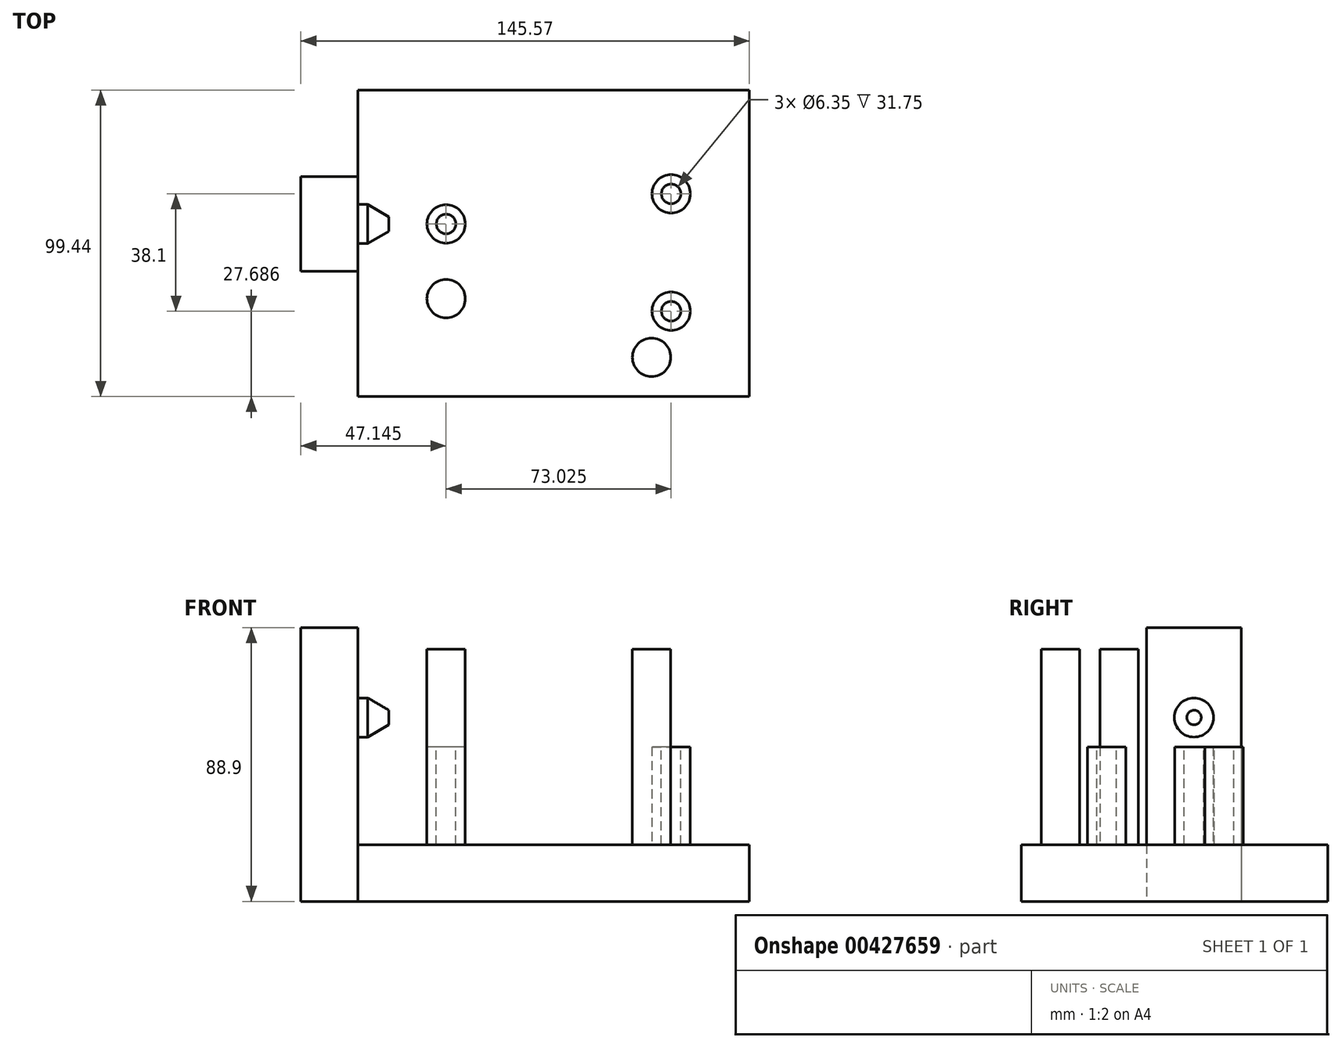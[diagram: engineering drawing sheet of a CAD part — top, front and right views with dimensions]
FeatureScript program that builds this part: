
annotation { "Feature Type Name" : "Feature", "Feature Type Description" : "" }
export const myFeature = defineFeature(function(context is Context, id is Id, definition is map)
    precondition{}
    {
        {
            var Q0;
            Q0=qCreatedBy(makeId("Top.planeOp"),FACE);
            var sketch = newSketch(context, id + "F0", { "sketchPlane" : qUnion([Q0])});
            skLineSegment(sketch, "E0.bottom", {"start": v(0, 0) * mm, "end": v(127, 0) * mm});
            skLineSegment(sketch, "E0.top", {"start": v(0, 99.44) * mm, "end": v(127, 99.44) * mm});
            skLineSegment(sketch, "E0.left", {"start": v(0, 0) * mm, "end": v(0, 99.44) * mm});
            skLineSegment(sketch, "E0.right", {"start": v(127, 0) * mm, "end": v(127, 99.44) * mm});
            skSolve(sketch);
        }
        {
            var Q0;
            Q0 = qSketchRegion(id + "F0", true);
            extrude(context, id + "F1", {"entities" : qUnion([Q0]), "depth" : 18.41 * mm});
        }
        {
            var Q0;
            Q0=qCreatedBy(makeId("Top.planeOp"),FACE);
            var sketch = newSketch(context, id + "F2", { "sketchPlane" : qUnion([Q0])});
            skLineSegment(sketch, "E1.bottom", {"start": v(0, 71.37) * mm, "end": v(-18.57, 71.37) * mm});
            skLineSegment(sketch, "E1.top", {"start": v(0, 40.64) * mm, "end": v(-18.57, 40.64) * mm});
            skLineSegment(sketch, "E1.left", {"start": v(0, 71.37) * mm, "end": v(0, 40.64) * mm});
            skLineSegment(sketch, "E1.right", {"start": v(-18.57, 71.37) * mm, "end": v(-18.57, 40.64) * mm});
            skSolve(sketch);
        }
        {
            var Q0;
            Q0 = qSketchRegion(id + "F2", true);
            extrude(context, id + "F3", {"entities" : qUnion([Q0]), "operationType" : NewBodyOperationType.ADD, "depth" : 88.9 * mm});
        }
        {
            var Q0;
            Q0=makeQuery(id+"F3.opExtrude","SWEPT_FACE",FACE,{"disambiguationData":[OSD([sQuery(id+"F2.wireOp",EDGE,"E1.top")])]});
            cPlane(context, id + "F4", {"entities" : qUnion([Q0]), "cplaneType" : CPlaneType.OFFSET, "offset" : 15.37 * mm, "oppositeDirection" : true, "width" : 152.4 * mm, "height" : 152.4 * mm});
        }
        {
            var Q0;
            Q0=qCreatedBy(id+"F4.planeOp",FACE);
            var sketch = newSketch(context, id + "F5", { "sketchPlane" : qUnion([Q0])});
            skLineSegment(sketch, "E2", {"start": v(0, 59.7) * mm, "end": v(0, 66.04) * mm});
            skLineSegment(sketch, "E3", {"start": v(0, 66.04) * mm, "end": v(3.17, 66.04) * mm});
            skLineSegment(sketch, "E4", {"start": v(3.17, 66.04) * mm, "end": v(10.03, 62.04) * mm});
            skLineSegment(sketch, "E5", {"start": v(10.03, 62.04) * mm, "end": v(10.03, 59.7) * mm});
            skLineSegment(sketch, "E6", {"start": v(0, 59.7) * mm, "end": v(10.03, 59.7) * mm});
            skSolve(sketch);
        }
        {
            var Q0;
            Q0 = qSketchRegion(id + "F5", true);
            var Q1;
            Q1=sQuery(id+"F5.wireOp",EDGE,"E6");
            revolve(context, id + "F6", {"operationType" : NewBodyOperationType.ADD, "entities" : qUnion([Q0]), "axis" : qUnion([Q1]), "revolveType" : RevolveType.FULL});
        }
        {
            var Q0;
            Q0=makeQuery(id+"F1.opExtrude","CAP_FACE",FACE,{"disambiguationData":[OSD([sQuery(id+"F0.wireOp",EDGE,"E0.bottom"),sQuery(id+"F0.wireOp",EDGE,"E0.top"),sQuery(id+"F0.wireOp",EDGE,"E0.left"),sQuery(id+"F0.wireOp",EDGE,"E0.right")])],"isStart":false});
            var sketch = newSketch(context, id + "F7", { "sketchPlane" : qUnion([Q0])});
            skCircle(sketch, "E7", {"center": v(95.25, 12.7) * mm, "radius": 6.22 * mm});
            skCircle(sketch, "E8", {"center": v(101.6, 27.69) * mm, "radius": 6.22 * mm});
            skCircle(sketch, "E9", {"center": v(101.6, 65.79) * mm, "radius": 6.22 * mm});
            skCircle(sketch, "E10", {"center": v(28.58, 56) * mm, "radius": 6.22 * mm});
            skCircle(sketch, "E11", {"center": v(28.58, 31.75) * mm, "radius": 6.22 * mm});
            skSolve(sketch);
        }
        {
            var Q0;
            Q0 = qSketchRegion(id + "F7", true);
            extrude(context, id + "F8", {"entities" : qUnion([Q0]), "operationType" : NewBodyOperationType.ADD, "depth" : 31.75 * mm});
        }
        {
            var Q0;
            Q0=makeQuery(id+"F8.opExtrude","CAP_FACE",FACE,{"disambiguationData":[OSD([sQuery(id+"F7.wireOp",EDGE,"E10")])],"isStart":false});
            var sketch = newSketch(context, id + "F9", { "sketchPlane" : qUnion([Q0])});
            skPoint(sketch, "E12", {"position": v(28.58, 56) * mm});
            skCircle(sketch, "E13.0", {"center": v(101.6, 65.79) * mm, "radius": 6.22 * mm, "construction": true});
            skCircle(sketch, "E14.0", {"center": v(101.6, 27.69) * mm, "radius": 6.22 * mm, "construction": true});
            skCircle(sketch, "E15", {"center": v(28.58, 56) * mm, "radius": 3.18 * mm});
            skCircle(sketch, "E16", {"center": v(101.6, 65.79) * mm, "radius": 3.18 * mm});
            skCircle(sketch, "E17", {"center": v(101.6, 27.69) * mm, "radius": 3.18 * mm});
            skSolve(sketch);
        }
        {
            var Q0;
            Q0=makeQuery(id+"F8.opExtrude","CAP_FACE",FACE,{"disambiguationData":[OSD([sQuery(id+"F7.wireOp",EDGE,"E11")])],"isStart":false});
            var sketch = newSketch(context, id + "F10", { "sketchPlane" : qUnion([Q0])});
            skCircle(sketch, "E18.0", {"center": v(95.25, 12.7) * mm, "radius": 6.22 * mm});
            skCircle(sketch, "E19.0", {"center": v(28.58, 31.75) * mm, "radius": 6.22 * mm});
            skSolve(sketch);
        }
        {
            var Q0;
            Q0 = qSketchRegion(id + "F10", true);
            extrude(context, id + "F11", {"entities" : qUnion([Q0]), "operationType" : NewBodyOperationType.ADD, "depth" : 31.75 * mm});
        }
        {
            var Q0;
            Q0 = qSketchRegion(id + "F9", true);
            extrude(context, id + "F12", {"entities" : qUnion([Q0]), "operationType" : NewBodyOperationType.REMOVE, "oppositeDirection" : true, "depth" : 31.75 * mm});
        }
    });
